# Revit family: Sirius Three WH - 50kW 60kW
name_source: partatom
category: Mechanical Equipment
units: mm (PartAtom-declared; Revit-internal decimal feet)

## family parameters
Always vertical = Yes
Cut with Voids When Loaded = No
OmniClass Number = 23.75.10.11.14.14
OmniClass Title = Condensing Boilers
Part Type = Normal
Room Calculation Point = No
Round Connector Dimension = Use Diameter
Shared = No
Work Plane-Based = No

## types (2) — shared parameters
6 Monthly = 0
Access Clearance Bottom = 500 mm  [stored 1.64042 ft]
Access Clearance Front = 400 mm  [stored 1.31234 ft]
Access Clearance Left = 20 mm  [stored 0.0656168 ft]
Access Clearance Right = 20 mm  [stored 0.0656168 ft]
Access Clearance Top = 300 mm
Air Inlet Connection Size = 125 mm  [stored 0.410105 ft]
Annually = Annual service according to manufacturers guidance.
BMS Links = Yes
Bespoke Timeframe = 0
Burner Control Type = Modulating
CE Mark = 0085CM0128
Colour = White
Condensate Drain Size = 22 mm  [stored 0.0721785 ft]
Condensate Drain Type = Plain
Configuration = Single boiler
Control Type = 0 - 10V, Volt free enable, Direct boiler weather compensating control system.
Daily = 0
Drain Connection Type = Plain
Embodied Carbon = 0
Environmental Product Declaration = 0
ErP Energy Label = A
External Material = Steel
Features = Compact and lightweight, the Sirius Three WH condensing boilers offer a market leading modulation ratio of 9:1 and comes with weather compensation as standard ensuring high seasonal efficiency all year round
Finish = Powder coated
Flow and Return Connection Size = 25 mm  [stored 0.082021 ft]
Flow and Return Connection Type = Threaded
Flue Connection size = 80 mm  [stored 0.262467 ft]
Flue or Air Intake Classification = C13; C33; B23
Frequency = 50 Hz
Fuel Connection Size = 20 mm  [stored 0.0656168 ft]
Fuel Connection Type = Threaded
Full Load Current = 0 A
Fuse Rating = 5 A
Green Guide for Specification = 0
Gross Weight = 40.00 kg
Heat Exchanger Material = Stainless Steel
Heater Operation = Condensing
Hydraulic Resistance at 11C temperature differential = 0.0
Hydraulic Resistance at 15C temperature differential = 0.0
IK Rating = 0
IP Rating = IPX5D
IfcExportAs = IfcBoilerType
IfcExportType = NOTDEFINED
Interlocks = Yes
Life Cycle Analysis = 0
Location of Manufacturer = 0
Maintenance Required 0 to 300hrs = 0
Maintenance Required 1001 to 2000hrs = 0
Maintenance Required 2001 to 4000hrs = 0
Maintenance Required 301 to 600hrs = 0
Maintenance Required 4001 to 8000hrs = 0
Maintenance Required 601 to 1000hrs = 0
Maintenance Required 8001 to 12000hrs = 0
Manufacturer = Potterton Commercial
Manufacturer Website = https://www.pottertoncommercial.co.uk
Material Ingredient Reporting = 0
Maximum Gas Inlet Pressure = 0.0 bar
Maximum Oil Inlet Pressure = 0.0 bar
Maximum Operating Pressure = 4.0 bar
Minimum Flow Rate at 11C temperature differential = 0.000 L/s
Minimum Flow Rate at 15C temperature differential = 0.000 L/s
Minimum Gas Inlet Pressure = 0.0 bar
Minimum Oil Inlet Pressure = 0.0 bar
Minimum Operating Pressure = 1.0 bar
Minimum Power Consumption = 0 W
Monthly = 0
Mounting = Wall Mounted
Nominal Gas Inlet Pressure = 0.0 bar
Nominal Oil Inlet Pressure = 0.0 bar
Operation and Maintenance Manual = https://www.pottertoncommercial.co.uk
Optional Fuel = Gas - LPG
Overall Height = 763 mm
Overall Length = 377 mm  [stored 1.23688 ft]
Overall Width = 450 mm  [stored 1.47638 ft]
Primary Fuel = Gas - NG
Product Literature = https://www.pottertoncommercial.co.uk
Quarterly = 0
Rated Criteria = 50/30
Reference Standard = EU/2016/426 GAR,  92/42/EEC, EN 15502-1, EN15502-2-1
Responsible Extraction of Materials = 0
Responsible Sourcing of Materials = 0
Safety Valve Connection Size = 20 mm  [stored 0.0656168 ft]
Safety Valve Connection Type = Threaded
Shape = Rectangular (Vertical)
Shipping Weight = 0.00 kg
Starting Current = 0 A
Supply Phase = 1
Turndown Ratio = 9:1
Uniclass2015 = Pr_60_60_08_34
Voltage = 230 V
Warranty ID = See manufacturers website for warranty options and T&C's
Water Treatment Required = Yes
Weekly = 0
zero-valued in all types: Access Clearance Rear, Default Elevation, Drain Connection Size, Oil Consumption rate

## per-type parameters (varying)
| type | Building Regulations Seasonal Efficiency | ErP Rated Efficiency at Full Load | ErP Rated Efficiency at Part Load | ErP Seasonal Efficiency | Gas Consumption rate | Hydraulic Resistance at 20C temperature differential | Maximum Power Consumption | Minimum Flow Rate at 20C temperature differential | NOx Emissions | Product Model Number | Product Range | Rated Output | Sound Pressure Level | Water Content |
| 60kW WH | 96.4 % | 94.61 % | 96.8 % | 92 % | 5.98 | 0.6 | 95 W | 0.660 L/s | 34.1 mg/kWh | 7705086 | Sirius Three WH 60kW | 59400 W | 59 dB | 5.0 L |
| 50kW WH | 96.6 % | 94.61 | 97.1 | 93 % | 4.9 | 0.5 | 80 W | 0.540 L/s | 29.8 mg/kWh | 7705085 | Sirius Three WH 50kW | 48600 W | 62 dB | 4.0 L |

note: source unit labels omitted for Hydraulic Resistance at 11C temperature differential, Hydraulic Resistance at 15C temperature differential, Hydraulic Resistance at 20C temperature differential — the stored unit's dimension contradicts the parameter name (converter mislabeling)

note: [stored X ft] marks values corroborated as IEEE doubles in the binary element streams (Revit-internal decimal feet)

## geometry (parser evidence)
native form markers: Blend x6, Sweep x8
no freeform markers — native parametric forms only
